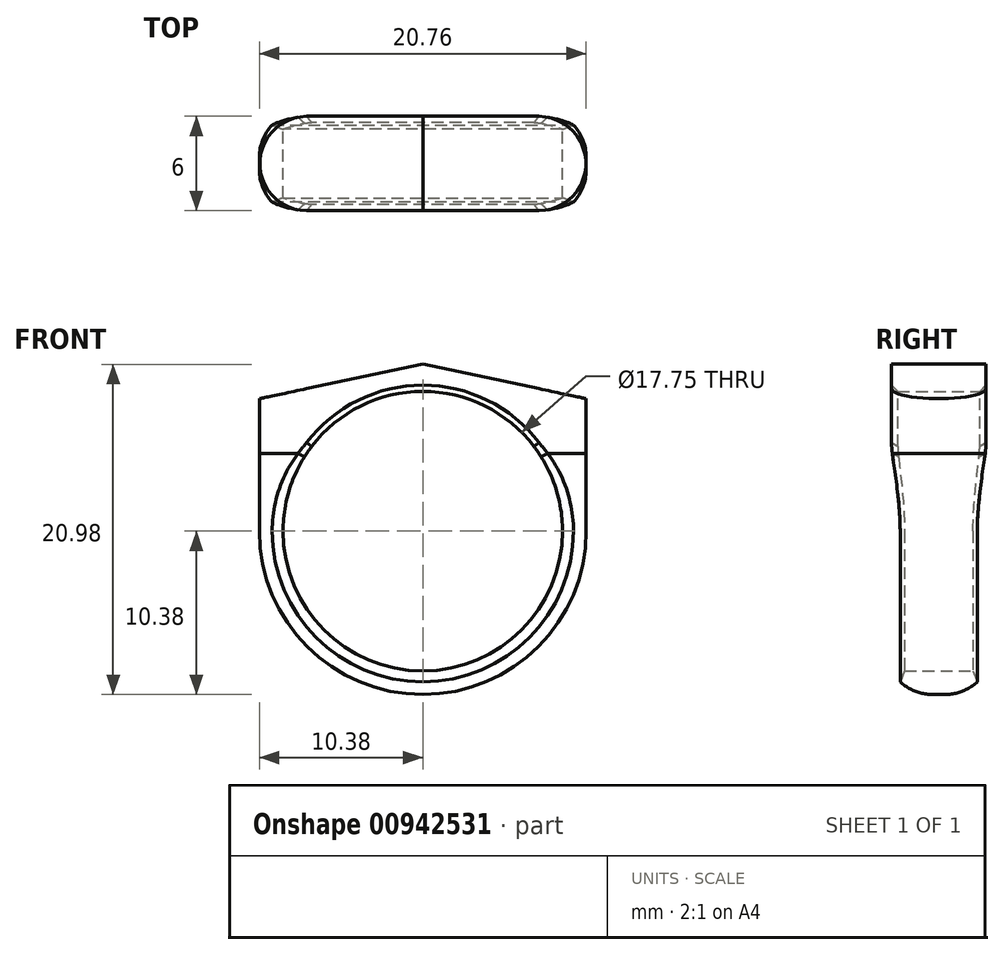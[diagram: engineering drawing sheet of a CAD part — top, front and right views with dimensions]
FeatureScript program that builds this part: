
annotation { "Feature Type Name" : "Feature", "Feature Type Description" : "" }
export const myFeature = defineFeature(function(context is Context, id is Id, definition is map)
    precondition{}
    {
        {
            var Q0;
            Q0=qCreatedBy(makeId("Front.planeOp"),FACE);
            var sketch = newSketch(context, id + "F0", { "sketchPlane" : qUnion([Q0])});
            skCircle(sketch, "E0", {"center": v(0, 0) * mm, "radius": 8.88 * mm});
            skCircle(sketch, "E1.0", {"center": v(0, 0) * mm, "radius": 10.38 * mm});
            skLineSegment(sketch, "E2", {"start": v(0, 10.6) * mm, "end": v(-10.38, 8.42) * mm});
            skLineSegment(sketch, "E3.MirrorCS", {"start": v(0, 10.6) * mm, "end": v(10.37, 8.42) * mm});
            skLineSegment(sketch, "E4", {"start": v(-10.38, 0) * mm, "end": v(-10.38, 8.42) * mm});
            skLineSegment(sketch, "E5.MirrorCS", {"start": v(10.38, 0) * mm, "end": v(10.38, 8.42) * mm});
            skPoint(sketch, "E6.orphan", {"position": v(-50.29, 0) * mm});
            skPoint(sketch, "E7.orphan", {"position": v(50.29, 0) * mm});
            skLineSegment(sketch, "E8", {"start": v(-0.1, 10.58) * mm, "end": v(0.1, 10.58) * mm});
            skLineSegment(sketch, "E9", {"start": v(0.1, 10.58) * mm, "end": v(0, 11.16) * mm});
            skLineSegment(sketch, "E10", {"start": v(-0.1, 10.58) * mm, "end": v(0, 11.16) * mm});
            skSolve(sketch);
        }
        {
            var Q0;
            {var subQ3=sQuery(id+"F0.wireOp",EDGE,"E5.MirrorCS");Q0=makeQuery(id+"F0.imprint","IMPRINT",FACE,{"disambiguationData":[TD([[makeQuery(id+"F0.imprint","IMPRINT",EDGE,{"derivedFrom":subQ3}),1.0]])]});}
            var Q1;
            {var subQ3=sQuery(id+"F0.wireOp",EDGE,"E4");Q1=makeQuery(id+"F0.imprint","IMPRINT",FACE,{"disambiguationData":[TD([[makeQuery(id+"F0.imprint","IMPRINT",EDGE,{"derivedFrom":subQ3}),-1.0]])]});}
            var Q2;
            Q2=makeQuery(id+"F0.imprint","IMPRINT",FACE,{"disambiguationData":[TD([[makeQuery(id+"F0.imprint","IMPRINT",EDGE,{"derivedFrom":sQuery(id+"F0.wireOp",EDGE,"E0")}),-1.0]])]});
            var Q3;
            {var subQ5=sQuery(id+"F0.wireOp",EDGE,"E8");Q3=makeQuery(id+"F0.imprint","IMPRINT",FACE,{"disambiguationData":[TD([[makeQuery(id+"F0.imprint","IMPRINT",EDGE,{"derivedFrom":subQ5}),-1.0]])]});}
            var Q4;
            {var subQ0=sQuery(id+"F0.wireOp",EDGE,"E8");Q4=makeQuery(id+"F0.imprint","IMPRINT",FACE,{"disambiguationData":[TD([[makeQuery(id+"F0.imprint","IMPRINT",EDGE,{"derivedFrom":subQ0}),1.0]])]});}
            extrude(context, id + "F1", {"entities" : qUnion([Q0, Q1, Q2, Q3, Q4]), "depth" : 3 * mm, "offsetDistance" : 25 * mm, "hasSecondDirection" : true, "secondDirectionOppositeDirection" : true, "secondDirectionDepth" : 3 * mm});
        }
        {
            var Q0;
            Q0=makeQuery(id+"F1.opExtrude","CAP_EDGE",EDGE,{"disambiguationData":[OSD([sQuery(id+"F0.wireOp",EDGE,"E5.MirrorCS")])],"isStart":false});
            var Q1;
            Q1=makeQuery(id+"F1.opExtrude","CAP_EDGE",EDGE,{"disambiguationData":[OSD([sQuery(id+"F0.wireOp",EDGE,"E5.MirrorCS")])],"isStart":true});
            fillet(context, id + "F2", {"entities" : qUnion([Q0, Q1]), "tangentPropagation" : true, "radius" : 3 * mm, "defaultsChanged" : false, "vertexSettings" : [], "allowEdgeOverflow" : false});
        }
        {
            var Q0;
            Q0=makeQuery(id+"F2.opFillet","BLEND_EDGE",EDGE,{"disambiguationData":[OD(0.0)],"blendedFrom":[makeQuery(id+"F1.opExtrude","CAP_EDGE",EDGE,{"disambiguationData":[OSD([sQuery(id+"F0.wireOp",EDGE,"E5.MirrorCS")])],"isStart":false}),makeQuery(id+"F1.opExtrude","SWEPT_FACE",FACE,{"disambiguationData":[OSD([sQuery(id+"F0.wireOp",EDGE,"E0")])]})],"blendedInto":[makeQuery(id+"F1.opExtrude","SWEPT_FACE",FACE,{"disambiguationData":[OSD([sQuery(id+"F0.wireOp",EDGE,"E0")])]})]});
            var Q1;
            Q1=makeQuery(id+"F2.opFillet","BLEND_EDGE",EDGE,{"disambiguationData":[OD(0.0)],"blendedFrom":[makeQuery(id+"F1.opExtrude","CAP_EDGE",EDGE,{"disambiguationData":[OSD([sQuery(id+"F0.wireOp",EDGE,"E4")])],"isStart":true}),makeQuery(id+"F1.opExtrude","SWEPT_FACE",FACE,{"disambiguationData":[OSD([sQuery(id+"F0.wireOp",EDGE,"E0")])]})],"blendedInto":[makeQuery(id+"F1.opExtrude","SWEPT_FACE",FACE,{"disambiguationData":[OSD([sQuery(id+"F0.wireOp",EDGE,"E0")])]})]});
            chamfer(context, id + "F3", {"entities" : qUnion([Q0, Q1]), "width" : 0.4 * mm, "tangentPropagation" : true});
        }
    });
